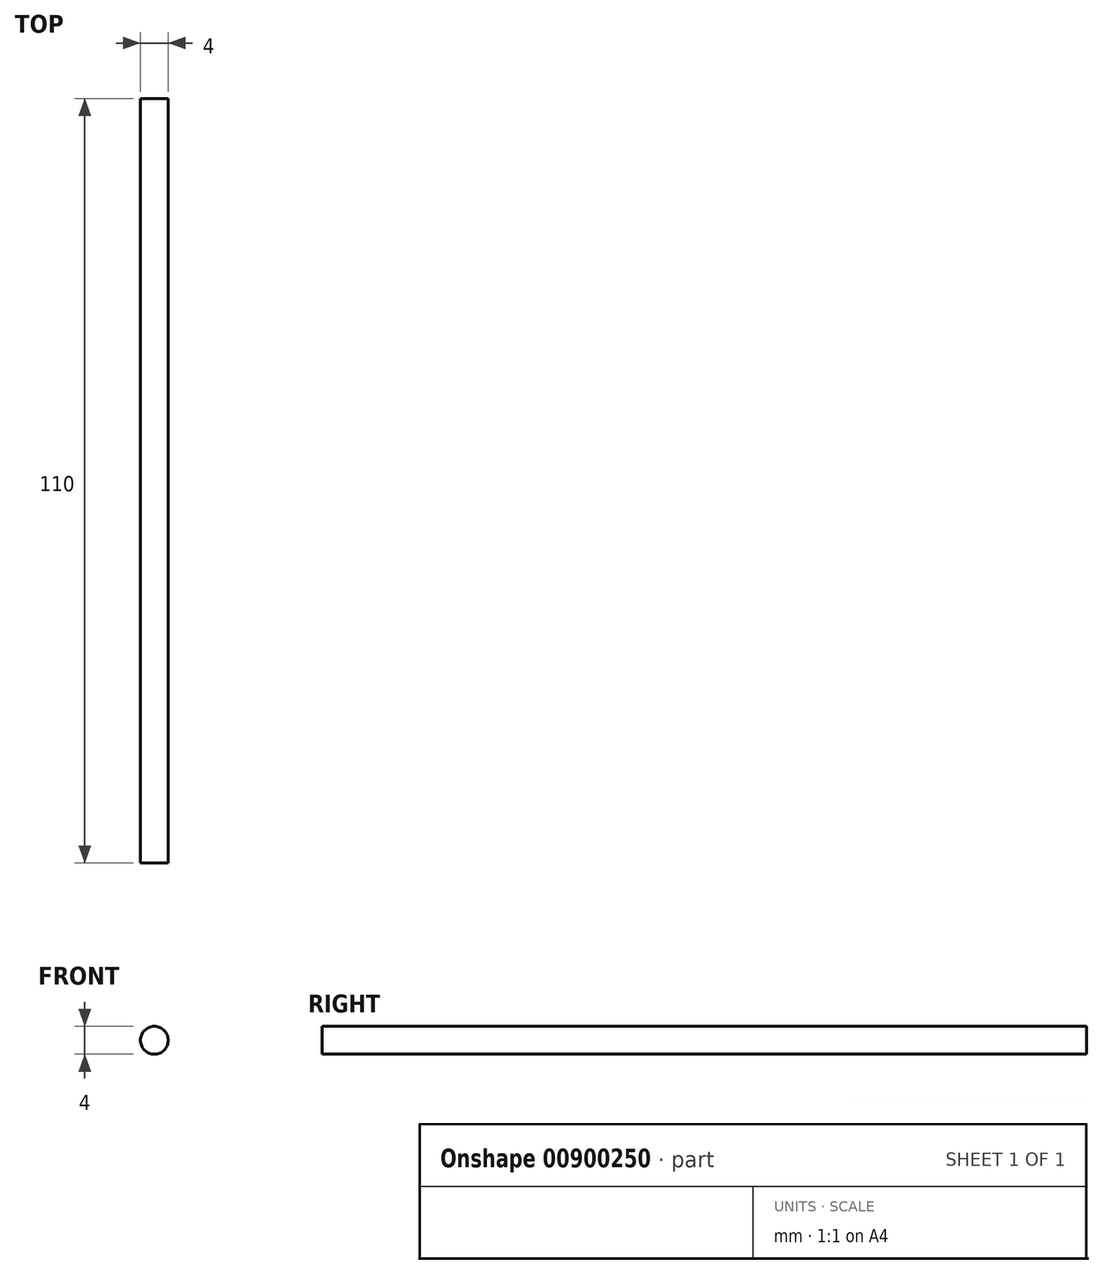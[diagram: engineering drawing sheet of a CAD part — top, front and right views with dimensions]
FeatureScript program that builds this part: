
annotation { "Feature Type Name" : "Feature", "Feature Type Description" : "" }
export const myFeature = defineFeature(function(context is Context, id is Id, definition is map)
    precondition{}
    {
        {
            var Q0;
            Q0=qCreatedBy(makeId("Front.planeOp"),FACE);
            var sketch = newSketch(context, id + "F0", { "sketchPlane" : qUnion([Q0])});
            skCircle(sketch, "E0", {"center": v(0, 0) * mm, "radius": 2 * mm});
            skSolve(sketch);
        }
        {
            var Q0;
            Q0=makeQuery(id+"F0.imprint","IMPRINT",FACE,{"disambiguationData":[TD([[makeQuery(id+"F0.imprint","IMPRINT",EDGE,{"derivedFrom":sQuery(id+"F0.wireOp",EDGE,"E0")}),1.0]])]});
            extrude(context, id + "F1", {"entities" : qUnion([Q0]), "endBound" : BoundingType.SYMMETRIC, "depth" : 110 * mm, "offsetDistance" : 25.4 * mm});
        }
    });
